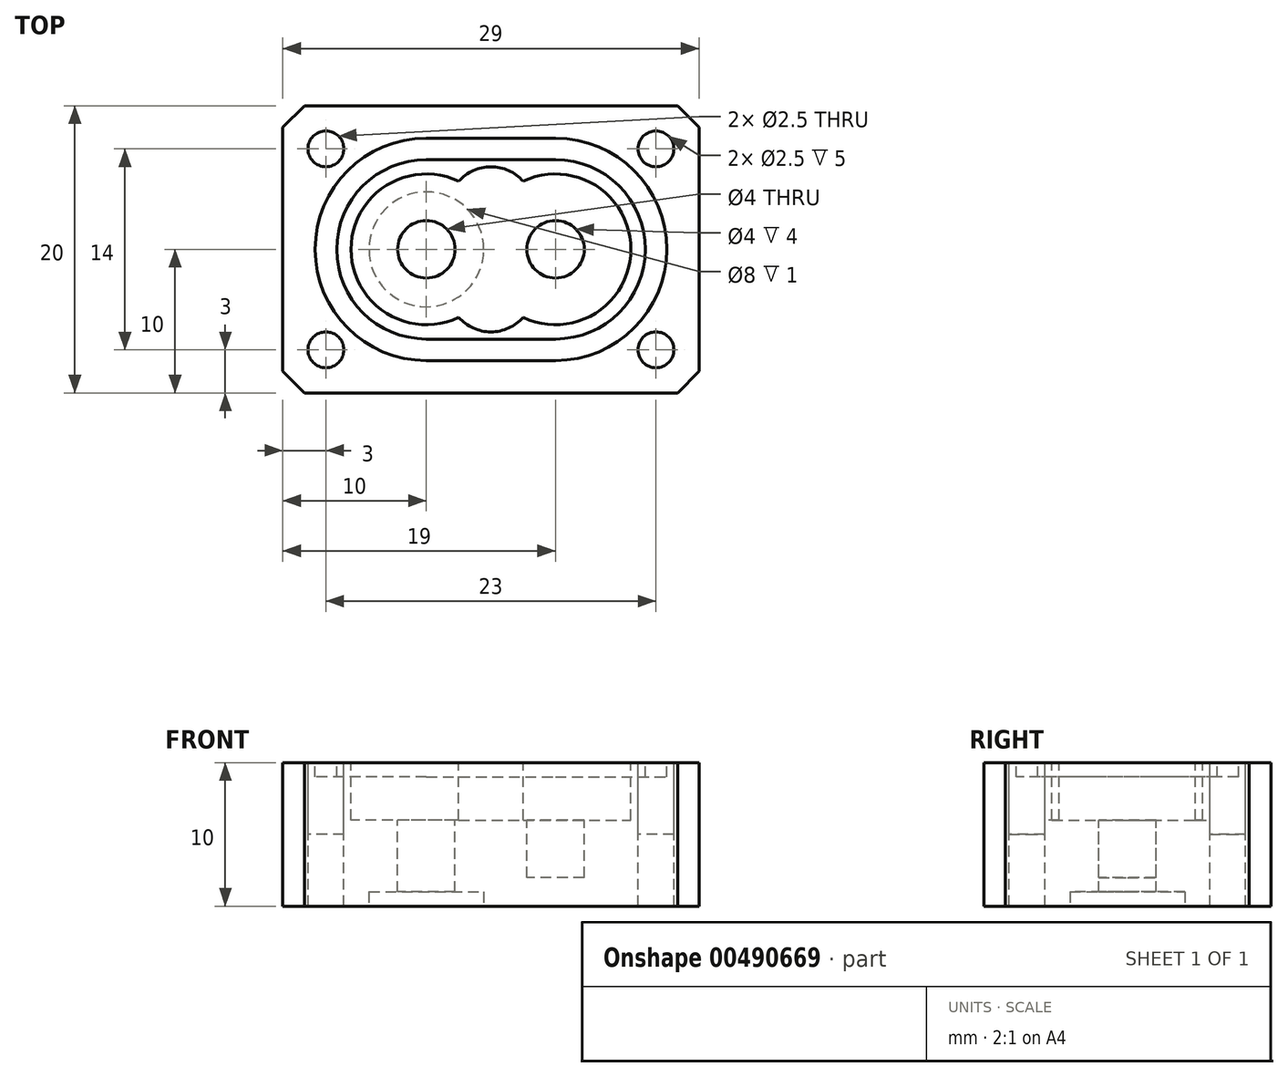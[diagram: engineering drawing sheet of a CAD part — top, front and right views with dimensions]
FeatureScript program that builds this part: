
annotation { "Feature Type Name" : "Feature", "Feature Type Description" : "" }
export const myFeature = defineFeature(function(context is Context, id is Id, definition is map)
    precondition{}
    {
        {
            var Q0;
            Q0=qCreatedBy(makeId("Top.planeOp"),FACE);
            var sketch = newSketch(context, id + "F0", { "sketchPlane" : qUnion([Q0])});
            skLineSegment(sketch, "E0.bottom", {"start": v(0, 0) * mm, "end": v(29, 0) * mm});
            skLineSegment(sketch, "E0.top", {"start": v(0, -20) * mm, "end": v(29, -20) * mm});
            skLineSegment(sketch, "E0.left", {"start": v(0, 0) * mm, "end": v(0, -20) * mm});
            skLineSegment(sketch, "E0.right", {"start": v(29, 0) * mm, "end": v(29, -20) * mm});
            skLineSegment(sketch, "E1", {"start": v(0, -10) * mm, "end": v(29, -10) * mm, "construction": true});
            skArc(sketch, "E2", {"start": v(16.74, -14.74) * mm, "mid": v(24.25, -10) * mm, "end": v(16.74, -5.26) * mm});
            skCircle(sketch, "E3", {"center": v(10, -10) * mm, "radius": 2 * mm});
            skCircle(sketch, "E4", {"center": v(19, -10) * mm, "radius": 2 * mm});
            skLineSegment(sketch, "E5", {"start": v(0, -3) * mm, "end": v(3, -3) * mm, "construction": true});
            skLineSegment(sketch, "E6", {"start": v(3, -3) * mm, "end": v(3, 0) * mm, "construction": true});
            skCircle(sketch, "E7", {"center": v(3, -3) * mm, "radius": 1.25 * mm});
            skPoint(sketch, "E8", {"position": v(14.5, -10) * mm});
            skCircle(sketch, "E9.0.1.0", {"center": v(3, -17) * mm, "radius": 1.25 * mm});
            skCircle(sketch, "E9.1.0.0", {"center": v(26, -3) * mm, "radius": 1.25 * mm});
            skCircle(sketch, "E9.1.1.0", {"center": v(26, -17) * mm, "radius": 1.25 * mm});
            skLineSegment(sketch, "E9.direction1", {"start": v(3, -3) * mm, "end": v(26, -3) * mm, "construction": true});
            skLineSegment(sketch, "E9.direction2", {"start": v(3, -3) * mm, "end": v(3, -17) * mm, "construction": true});
            skArc(sketch, "E10", {"start": v(10, -3.75) * mm, "mid": v(3.75, -10) * mm, "end": v(10, -16.25) * mm});
            skArc(sketch, "E11", {"start": v(19, -16.25) * mm, "mid": v(25.25, -10) * mm, "end": v(19, -3.75) * mm});
            skLineSegment(sketch, "E12", {"start": v(10, -3.75) * mm, "end": v(19, -3.75) * mm});
            skLineSegment(sketch, "E13", {"start": v(10, -16.25) * mm, "end": v(19, -16.25) * mm});
            skLineSegment(sketch, "E14.0", {"start": v(10, -17.75) * mm, "end": v(19, -17.75) * mm});
            skArc(sketch, "E14.1", {"start": v(10, -2.25) * mm, "mid": v(2.25, -10) * mm, "end": v(10, -17.75) * mm});
            skLineSegment(sketch, "E14.2", {"start": v(10, -2.25) * mm, "end": v(19, -2.25) * mm});
            skArc(sketch, "E14.3", {"start": v(19, -17.75) * mm, "mid": v(26.75, -10) * mm, "end": v(19, -2.25) * mm});
            skLineSegment(sketch, "E15", {"start": v(0, -7.25) * mm, "end": v(29, -7.25) * mm, "construction": true});
            skLineSegment(sketch, "E16", {"start": v(0, -12.75) * mm, "end": v(29, -12.75) * mm, "construction": true});
            skArc(sketch, "E17", {"start": v(16.74, -5.26) * mm, "mid": v(14.5, -4.25) * mm, "end": v(12.26, -5.26) * mm});
            skArc(sketch, "E18", {"start": v(12.26, -14.74) * mm, "mid": v(14.5, -15.75) * mm, "end": v(16.74, -14.74) * mm});
            skArc(sketch, "E19.trimOffspring", {"start": v(12.26, -5.26) * mm, "mid": v(4.75, -10) * mm, "end": v(12.26, -14.74) * mm});
            skArc(sketch, "E20.0", {"start": v(10, -2.95) * mm, "mid": v(2.95, -10) * mm, "end": v(10, -17.05) * mm, "construction": true});
            skLineSegment(sketch, "E20.1", {"start": v(10, -2.95) * mm, "end": v(19, -2.95) * mm, "construction": true});
            skArc(sketch, "E20.2", {"start": v(19, -17.05) * mm, "mid": v(26.05, -10) * mm, "end": v(19, -2.95) * mm, "construction": true});
            skLineSegment(sketch, "E20.3", {"start": v(10, -17.05) * mm, "end": v(19, -17.05) * mm, "construction": true});
            skSolve(sketch);
        }
        {
            var Q0;
            Q0=makeQuery(id+"F0.imprint","IMPRINT",FACE,{"disambiguationData":[TD([[makeQuery(id+"F0.imprint","IMPRINT",EDGE,{"derivedFrom":sQuery(id+"F0.wireOp",EDGE,"E0.bottom")}),-1.0]])]});
            var Q1;
            Q1=makeQuery(id+"F0.imprint","IMPRINT",FACE,{"disambiguationData":[TD([[makeQuery(id+"F0.imprint","IMPRINT",EDGE,{"derivedFrom":sQuery(id+"F0.wireOp",EDGE,"MZw8L1mY-04MB-L0nq-oH4W-q9KqwQQnYDyC")}),-1.0]])]});
            var Q2;
            Q2=makeQuery(id+"F0.imprint","IMPRINT",FACE,{"disambiguationData":[TD([[makeQuery(id+"F0.imprint","IMPRINT",EDGE,{"derivedFrom":sQuery(id+"F0.wireOp",EDGE,"MZw8L1mY-04MB-L0nq-oH4W-q9KqwQQnYDyC")}),1.0]])]});
            var Q3;
            Q3=makeQuery(id+"F0.imprint","IMPRINT",FACE,{"disambiguationData":[TD([[makeQuery(id+"F0.imprint","IMPRINT",EDGE,{"derivedFrom":sQuery(id+"F0.wireOp",EDGE,"E4")}),1.0]])]});
            var Q4;
            Q4=makeQuery(id+"F0.imprint","IMPRINT",FACE,{"disambiguationData":[TD([[makeQuery(id+"F0.imprint","IMPRINT",EDGE,{"derivedFrom":sQuery(id+"F0.wireOp",EDGE,"E10")}),-1.0]])]});
            var Q5;
            Q5=makeQuery(id+"F0.imprint","IMPRINT",FACE,{"disambiguationData":[TD([[makeQuery(id+"F0.imprint","IMPRINT",EDGE,{"derivedFrom":sQuery(id+"F0.wireOp",EDGE,"E2")}),1.0]])]});
            var Q6;
            Q6=makeQuery(id+"F0.imprint","IMPRINT",FACE,{"disambiguationData":[TD([[makeQuery(id+"F0.imprint","IMPRINT",EDGE,{"derivedFrom":sQuery(id+"F0.wireOp",EDGE,"E2")}),-1.0]])]});
            var Q7;
            Q7=makeQuery(id+"F0.imprint","IMPRINT",FACE,{"disambiguationData":[TD([[makeQuery(id+"F0.imprint","IMPRINT",EDGE,{"derivedFrom":sQuery(id+"F0.wireOp",EDGE,"E9.0.1.0")}),1.0]])]});
            var Q8;
            Q8=makeQuery(id+"F0.imprint","IMPRINT",FACE,{"disambiguationData":[TD([[makeQuery(id+"F0.imprint","IMPRINT",EDGE,{"derivedFrom":sQuery(id+"F0.wireOp",EDGE,"E9.1.0.0")}),1.0]])]});
            extrude(context, id + "F1", {"entities" : qUnion([Q0, Q1, Q2, Q3, Q4, Q5, Q6, Q7, Q8]), "oppositeDirection" : true, "depth" : 10 * mm, "offsetDistance" : 25 * mm});
        }
        {
            var Q0;
            Q0=makeQuery(id+"F0.imprint","IMPRINT",FACE,{"disambiguationData":[TD([[makeQuery(id+"F0.imprint","IMPRINT",EDGE,{"derivedFrom":sQuery(id+"F0.wireOp",EDGE,"E7")}),1.0]])]});
            var Q1;
            Q1=makeQuery(id+"F0.imprint","IMPRINT",FACE,{"disambiguationData":[TD([[makeQuery(id+"F0.imprint","IMPRINT",EDGE,{"derivedFrom":sQuery(id+"F0.wireOp",EDGE,"E9.1.0.0")}),1.0]])]});
            var Q2;
            Q2=makeQuery(id+"F0.imprint","IMPRINT",FACE,{"disambiguationData":[TD([[makeQuery(id+"F0.imprint","IMPRINT",EDGE,{"derivedFrom":sQuery(id+"F0.wireOp",EDGE,"E9.1.1.0")}),1.0]])]});
            var Q3;
            Q3=makeQuery(id+"F0.imprint","IMPRINT",FACE,{"disambiguationData":[TD([[makeQuery(id+"F0.imprint","IMPRINT",EDGE,{"derivedFrom":sQuery(id+"F0.wireOp",EDGE,"E9.0.1.0")}),1.0]])]});
            extrude(context, id + "F2", {"entities" : qUnion([Q0, Q1, Q2, Q3]), "operationType" : NewBodyOperationType.REMOVE, "oppositeDirection" : true, "depth" : 5 * mm, "offsetDistance" : 25 * mm});
        }
        {
            var Q0;
            Q0=makeQuery(id+"F0.imprint","IMPRINT",FACE,{"disambiguationData":[TD([[makeQuery(id+"F0.imprint","IMPRINT",EDGE,{"derivedFrom":sQuery(id+"F0.wireOp",EDGE,"E10")}),-1.0]])]});
            extrude(context, id + "F3", {"entities" : qUnion([Q0]), "operationType" : NewBodyOperationType.REMOVE, "oppositeDirection" : true, "depth" : 1 * mm, "offsetDistance" : 25 * mm});
        }
        {
            var Q0;
            Q0=makeQuery(id+"F0.imprint","IMPRINT",FACE,{"disambiguationData":[TD([[makeQuery(id+"F0.imprint","IMPRINT",EDGE,{"derivedFrom":sQuery(id+"F0.wireOp",EDGE,"E4")}),1.0]])]});
            extrude(context, id + "F4", {"entities" : qUnion([Q0]), "operationType" : NewBodyOperationType.REMOVE, "oppositeDirection" : true, "depth" : 8 * mm, "offsetDistance" : 25 * mm});
        }
        {
            var Q0;
            Q0=makeQuery(id+"F0.imprint","IMPRINT",FACE,{"disambiguationData":[TD([[makeQuery(id+"F0.imprint","IMPRINT",EDGE,{"derivedFrom":sQuery(id+"F0.wireOp",EDGE,"E2")}),1.0]])]});
            extrude(context, id + "F5", {"entities" : qUnion([Q0]), "operationType" : NewBodyOperationType.REMOVE, "oppositeDirection" : true, "depth" : 4 * mm, "offsetDistance" : 25 * mm});
        }
        {
            var Q0;
            Q0=makeQuery(id+"F1.opExtrude","CAP_FACE",FACE,{"disambiguationData":[OSD([sQuery(id+"F0.wireOp",EDGE,"E0.bottom"),sQuery(id+"F0.wireOp",EDGE,"E0.top"),sQuery(id+"F0.wireOp",EDGE,"E0.left"),sQuery(id+"F0.wireOp",EDGE,"E0.right"),sQuery(id+"F0.wireOp",EDGE,"E3"),sQuery(id+"F0.wireOp",EDGE,"E7"),sQuery(id+"F0.wireOp",EDGE,"E9.0.1.0"),sQuery(id+"F0.wireOp",EDGE,"E9.1.0.0"),sQuery(id+"F0.wireOp",EDGE,"E9.1.1.0")])],"isStart":false});
            var sketch = newSketch(context, id + "F6", { "sketchPlane" : qUnion([Q0])});
            skLineSegment(sketch, "E21", {"start": v(14.5, 0) * mm, "end": v(14.5, 20) * mm, "construction": true});
            skCircle(sketch, "E22", {"center": v(14.5, 3) * mm, "radius": 1.25 * mm});
            skCircle(sketch, "E23", {"center": v(14.5, 17) * mm, "radius": 1.25 * mm});
            skCircle(sketch, "E24", {"center": v(10, 10) * mm, "radius": 4 * mm});
            skSolve(sketch);
        }
        {
            var Q0;
            Q0=makeQuery(id+"F6.imprint","IMPRINT",FACE,{"disambiguationData":[TD([[makeQuery(id+"F6.imprint","IMPRINT",EDGE,{"derivedFrom":sQuery(id+"F6.wireOp",EDGE,"E24")}),1.0]])]});
            extrude(context, id + "F7", {"entities" : qUnion([Q0]), "operationType" : NewBodyOperationType.REMOVE, "oppositeDirection" : true, "depth" : 1 * mm, "offsetDistance" : 25 * mm});
        }
        {
            var Q0;
            Q0=makeQuery(id+"F1.opExtrude","SWEPT_EDGE",EDGE,{"disambiguationData":[OSD([sQuery(id+"F0.wireOp",EDGE,"E0.top"),sQuery(id+"F0.wireOp",EDGE,"E0.right")])]});
            var Q1;
            Q1=makeQuery(id+"F1.opExtrude","SWEPT_EDGE",EDGE,{"disambiguationData":[OSD([sQuery(id+"F0.wireOp",EDGE,"E0.top"),sQuery(id+"F0.wireOp",EDGE,"E0.left")])]});
            var Q2;
            Q2=makeQuery(id+"F1.opExtrude","SWEPT_EDGE",EDGE,{"disambiguationData":[OSD([sQuery(id+"F0.wireOp",EDGE,"E0.bottom"),sQuery(id+"F0.wireOp",EDGE,"E0.left")])]});
            var Q3;
            Q3=makeQuery(id+"F1.opExtrude","SWEPT_EDGE",EDGE,{"disambiguationData":[OSD([sQuery(id+"F0.wireOp",EDGE,"E0.bottom"),sQuery(id+"F0.wireOp",EDGE,"E0.right")])]});
            chamfer(context, id + "F8", {"entities" : qUnion([Q0, Q1, Q2, Q3]), "width" : 1.5 * mm, "tangentPropagation" : true});
        }
    });
